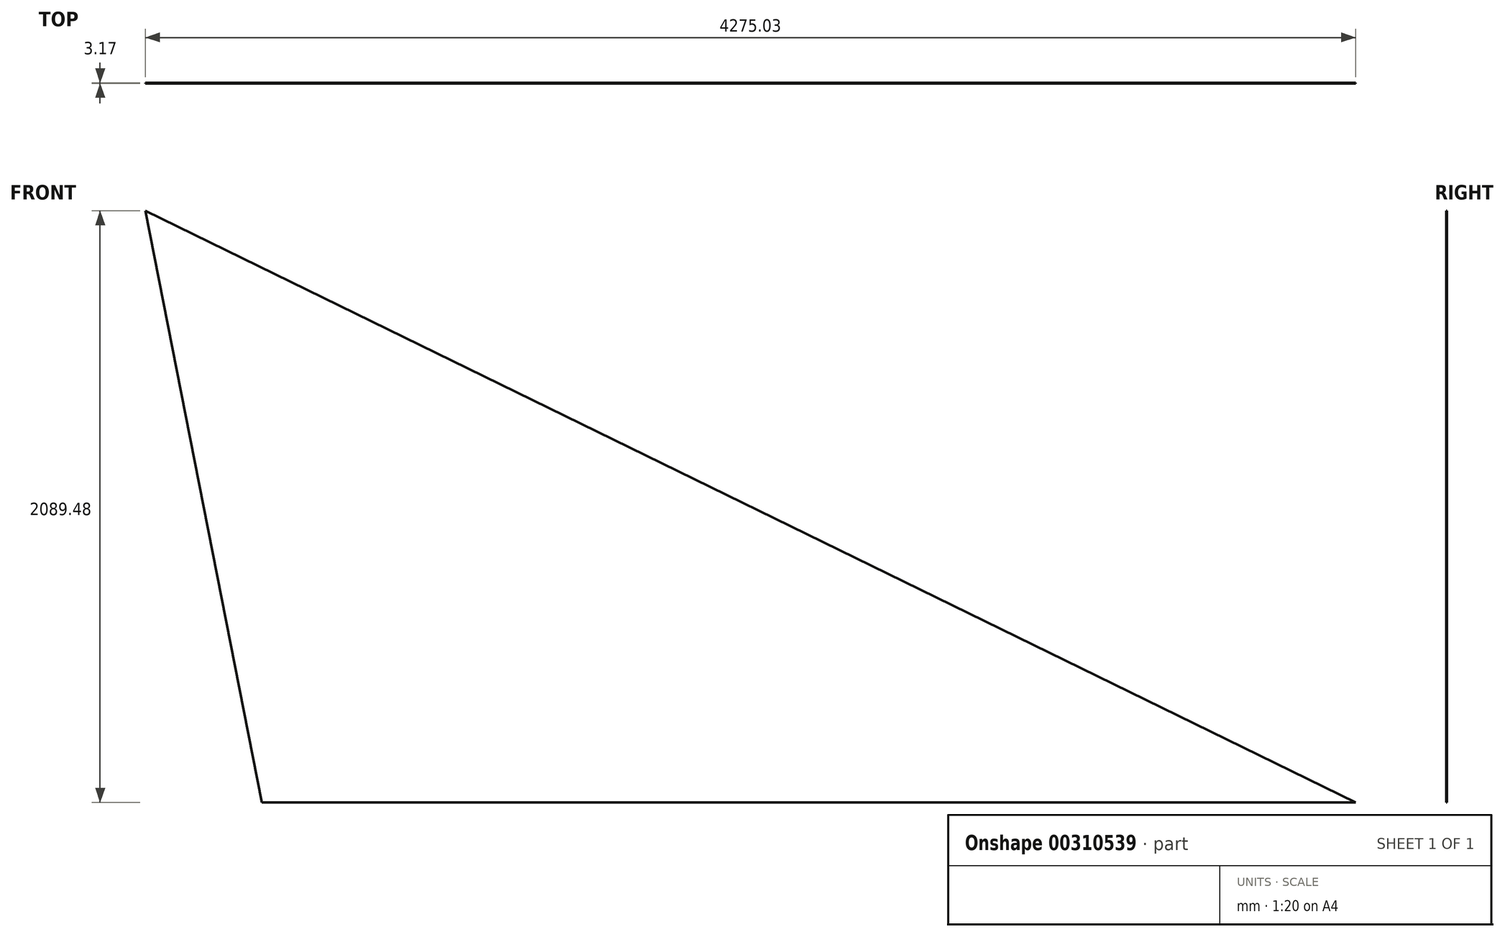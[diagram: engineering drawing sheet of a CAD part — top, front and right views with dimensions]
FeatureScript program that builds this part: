
annotation { "Feature Type Name" : "Feature", "Feature Type Description" : "" }
export const myFeature = defineFeature(function(context is Context, id is Id, definition is map)
    precondition{}
    {
        {
            var Q0;
            Q0=qCreatedBy(makeId("Front.planeOp"),FACE);
            var sketch = newSketch(context, id + "F0", { "sketchPlane" : qUnion([Q0])});
            skLineSegment(sketch, "E0.0", {"start": v(-431.42, 2064.08) * mm, "end": v(3843.61, -25.4) * mm});
            skLineSegment(sketch, "E0.1", {"start": v(-20.9, -25.4) * mm, "end": v(-431.42, 2064.08) * mm});
            skLineSegment(sketch, "E0.2", {"start": v(-20.9, -25.4) * mm, "end": v(3843.61, -25.4) * mm});
            skSolve(sketch);
        }
        {
            var Q0;
            Q0 = qSketchRegion(id + "F0", true);
            extrude(context, id + "F1", {"entities" : qUnion([Q0]), "depth" : 3.17 * mm});
        }
    });
